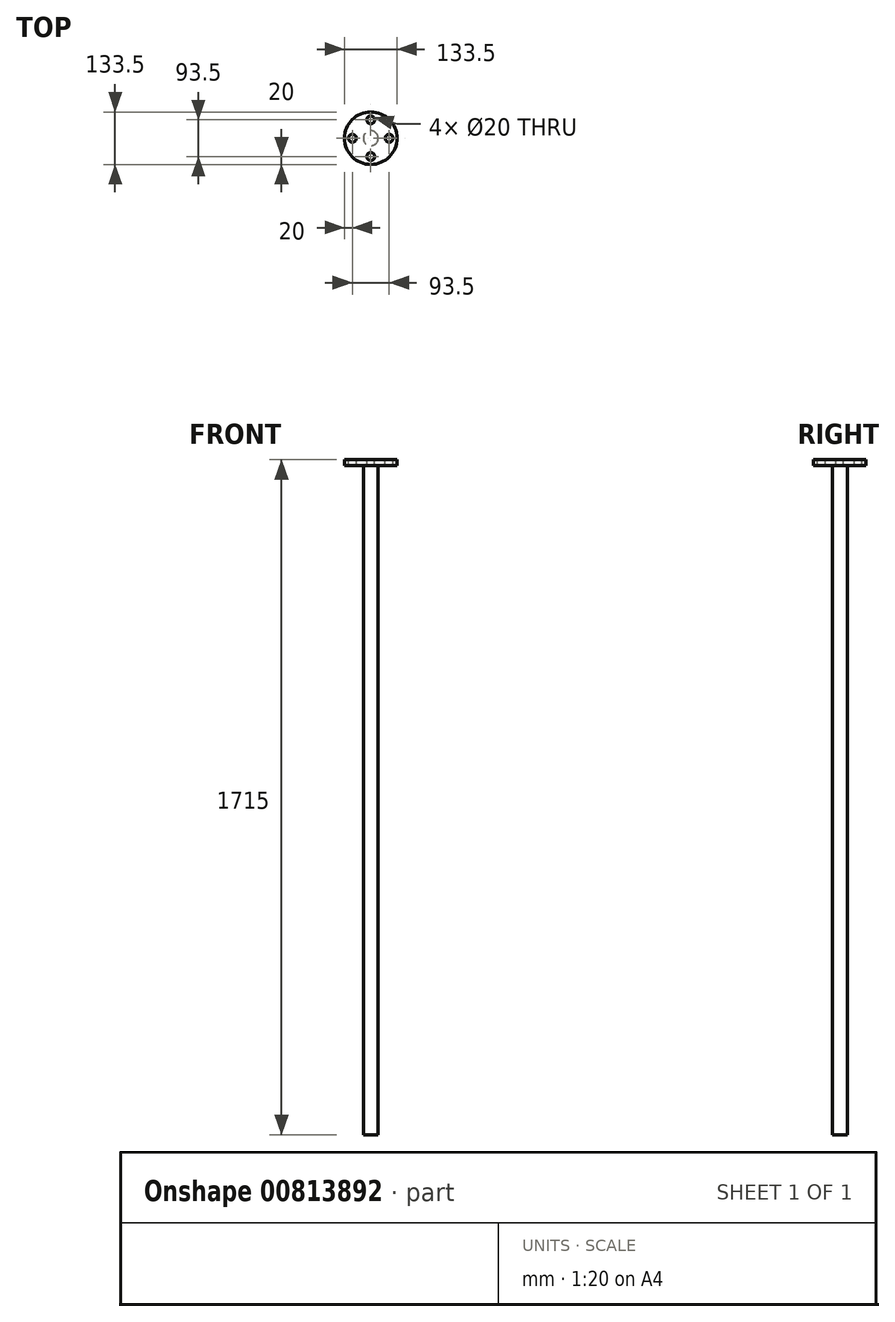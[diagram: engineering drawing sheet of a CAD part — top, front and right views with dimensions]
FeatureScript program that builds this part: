
annotation { "Feature Type Name" : "Feature", "Feature Type Description" : "" }
export const myFeature = defineFeature(function(context is Context, id is Id, definition is map)
    precondition{}
    {
        {
            var Q0;
            Q0=qCreatedBy(makeId("Top.planeOp"),FACE);
            var sketch = newSketch(context, id + "F0", { "sketchPlane" : qUnion([Q0])});
            skCircle(sketch, "E0", {"center": v(0, 0) * mm, "radius": 66.75 * mm});
            skSolve(sketch);
        }
        {
            var Q0;
            Q0 = qSketchRegion(id + "F0", true);
            extrude(context, id + "F1", {"entities" : qUnion([Q0]), "depth" : 15 * mm, "offsetDistance" : 25.4 * mm});
        }
        {
            var Q0;
            Q0=makeQuery(id+"F1.opExtrude","CAP_FACE",FACE,{"disambiguationData":[OSD([sQuery(id+"F0.wireOp",EDGE,"E0")])],"isStart":true});
            var sketch = newSketch(context, id + "F2", { "sketchPlane" : qUnion([Q0])});
            skCircle(sketch, "E1", {"center": v(0, 0) * mm, "radius": 19 * mm});
            skSolve(sketch);
        }
        {
            var Q0;
            Q0 = qSketchRegion(id + "F2", true);
            extrude(context, id + "F3", {"entities" : qUnion([Q0]), "depth" : 1700 * mm, "offsetDistance" : 25.4 * mm});
        }
        {
            var Q0;
            Q0=makeQuery(id+"F1.opExtrude","CAP_FACE",FACE,{"disambiguationData":[OSD([sQuery(id+"F0.wireOp",EDGE,"E0")])],"isStart":false});
            var sketch = newSketch(context, id + "F4", { "sketchPlane" : qUnion([Q0])});
            skCircle(sketch, "E2", {"center": v(0, 0) * mm, "radius": 46.75 * mm, "construction": true});
            skCircle(sketch, "E3", {"center": v(46.75, 0) * mm, "radius": 10 * mm});
            skCircle(sketch, "E4.1.1", {"center": v(0, 46.75) * mm, "radius": 10 * mm});
            skCircle(sketch, "E4.2.1", {"center": v(-46.75, 0) * mm, "radius": 10 * mm});
            skCircle(sketch, "E4.3.1", {"center": v(0, -46.75) * mm, "radius": 10 * mm});
            skSolve(sketch);
        }
        {
            var Q0;
            Q0 = qSketchRegion(id + "F4", true);
            extrude(context, id + "F5", {"entities" : qUnion([Q0]), "operationType" : NewBodyOperationType.REMOVE, "endBound" : BoundingType.UP_TO_NEXT, "oppositeDirection" : true, "depth" : 25.4 * mm, "offsetDistance" : 25.4 * mm});
        }
    });
